# Revit family: RW3021-A15_6-EC
name_source: partatom
category: Mechanical Equipment
revit_build: Autodesk Revit 2018 (Build: 20170223_1515(x64)
units: mm (PartAtom-declared; Revit-internal decimal feet)

## family parameters
Always vertical = Yes
Cut with Voids When Loaded = No
Part Type = Normal
Room Calculation Point = No
Round Connector Dimension = Use Diameter
Shared = No
Work Plane-Based = No

## types (1)
- RW3021-A15/6-EC
    Cable Length (m) = As Per Specification
    Cable Tyoe = HO7RN
    Description = The RW is Sulzer’s standard range of submersible mixers, economical without compromising on reliable design. These compact, versatile submersible mixers are ideal for agitating, blending, mixing, dissolving, and suspension of solids in municipal treatment plants, industry, and agriculture. The RW mixers can easily be fitted to existing guiderails and lifting devices without modification, using our wide range of brackets and adapters.
    Fasteners = Stainless steel 1.4401 (AISI 316)
    Manufacturer = Sulzer
    Model = Type ABS RW
    Motor Housing = Cast Iron EN-GJL-250
    Motor Power (kW) = P1=1.5
    Motor Shaft = Stainless steel 1.4021 (AISI 420)
    Product Specification Link = https://www.sulzer.com
    Propeller = 1.4460 (AISI 329)
    Rated Current (A) = 4.6
    Rated Voltage (V) = 400
    Speed (r/min) = 904
    mixing capacity (up to m3/s) = 0.83 m³

## geometry (parser evidence)
native form markers: Sweep x3
no freeform markers — native parametric forms only
